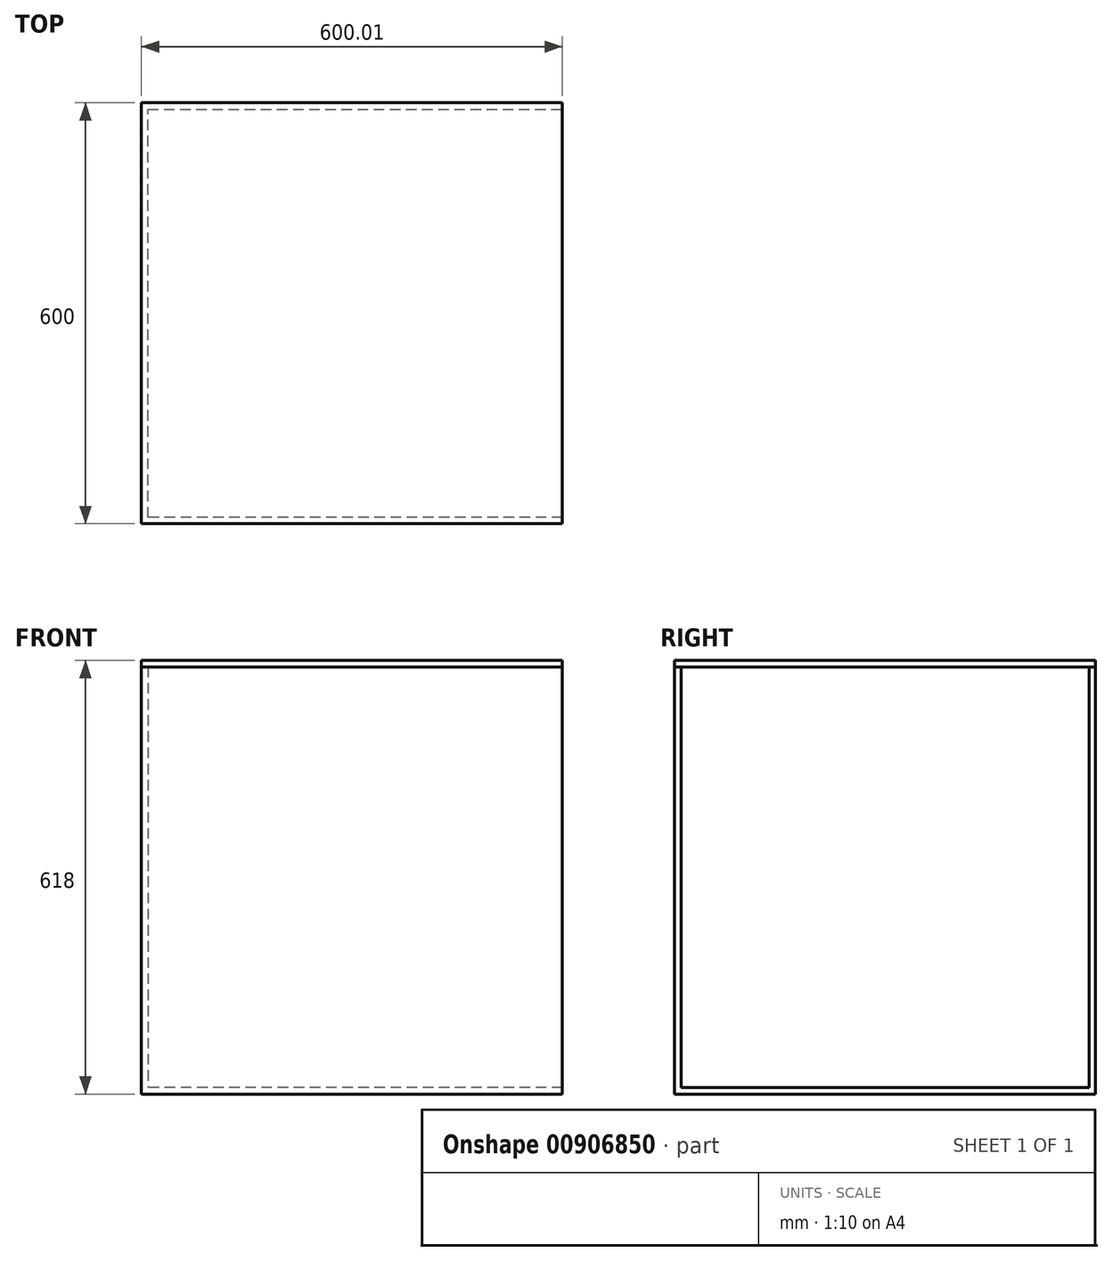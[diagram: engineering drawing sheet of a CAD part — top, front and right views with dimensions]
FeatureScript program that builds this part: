
annotation { "Feature Type Name" : "Feature", "Feature Type Description" : "" }
export const myFeature = defineFeature(function(context is Context, id is Id, definition is map)
    precondition{}
    {
        {
            var Q0;
            Q0=qCreatedBy(makeId("Top.planeOp"),FACE);
            var sketch = newSketch(context, id + "F0", { "sketchPlane" : qUnion([Q0])});
            skLineSegment(sketch, "E0.bottom", {"start": v(5.9, 0) * mm, "end": v(605.9, 0) * mm});
            skLineSegment(sketch, "E0.top", {"start": v(5.9, 600) * mm, "end": v(605.9, 600) * mm});
            skLineSegment(sketch, "E0.left", {"start": v(5.9, 0) * mm, "end": v(5.9, 600) * mm});
            skLineSegment(sketch, "E0.right", {"start": v(605.9, 0) * mm, "end": v(605.9, 600) * mm});
            skSolve(sketch);
        }
        {
            var Q0;
            Q0=makeQuery(id+"F0.imprint","IMPRINT",FACE,{"disambiguationData":[TD([[makeQuery(id+"F0.imprint","IMPRINT",EDGE,{"derivedFrom":sQuery(id+"F0.wireOp",EDGE,"E0.bottom")}),1.0]])]});
            extrude(context, id + "F1", {"entities" : qUnion([Q0]), "depth" : 9 * mm, "offsetDistance" : 25 * mm});
        }
        {
            var Q0;
            Q0=makeQuery(id+"F1.opExtrude","CAP_FACE",FACE,{"disambiguationData":[OSD([sQuery(id+"F0.wireOp",EDGE,"E0.bottom"),sQuery(id+"F0.wireOp",EDGE,"E0.top"),sQuery(id+"F0.wireOp",EDGE,"E0.left"),sQuery(id+"F0.wireOp",EDGE,"E0.right")])],"isStart":false});
            var sketch = newSketch(context, id + "F2", { "sketchPlane" : qUnion([Q0])});
            skLineSegment(sketch, "E1.bottom", {"start": v(5.9, 0) * mm, "end": v(14.9, 0) * mm});
            skLineSegment(sketch, "E1.top", {"start": v(5.9, 600) * mm, "end": v(14.9, 600) * mm});
            skLineSegment(sketch, "E1.left", {"start": v(5.9, 0) * mm, "end": v(5.9, 600) * mm});
            skLineSegment(sketch, "E1.right", {"start": v(14.9, 0) * mm, "end": v(14.9, 600) * mm});
            skSolve(sketch);
        }
        {
            var Q0;
            Q0 = qSketchRegion(id + "F2", true);
            extrude(context, id + "F3", {"entities" : qUnion([Q0]), "depth" : 600 * mm, "offsetDistance" : 25 * mm});
        }
        {
            var Q0;
            Q0=makeQuery(id+"F1.opExtrude","CAP_FACE",FACE,{"disambiguationData":[OSD([sQuery(id+"F0.wireOp",EDGE,"E0.bottom"),sQuery(id+"F0.wireOp",EDGE,"E0.top"),sQuery(id+"F0.wireOp",EDGE,"E0.left"),sQuery(id+"F0.wireOp",EDGE,"E0.right")])],"isStart":false});
            var sketch = newSketch(context, id + "F4", { "sketchPlane" : qUnion([Q0])});
            skLineSegment(sketch, "E2.bottom", {"start": v(14.9, 600) * mm, "end": v(605.9, 600) * mm});
            skLineSegment(sketch, "E2.top", {"start": v(14.9, 591) * mm, "end": v(605.9, 591) * mm});
            skLineSegment(sketch, "E2.left", {"start": v(14.9, 600) * mm, "end": v(14.9, 591) * mm});
            skLineSegment(sketch, "E2.right", {"start": v(605.9, 600) * mm, "end": v(605.9, 591) * mm});
            skSolve(sketch);
        }
        {
            var Q0;
            Q0 = qSketchRegion(id + "F4", true);
            extrude(context, id + "F5", {"entities" : qUnion([Q0]), "operationType" : NewBodyOperationType.ADD, "depth" : 600 * mm, "offsetDistance" : 25 * mm});
        }
        {
            var Q0;
            Q0=makeQuery(id+"F1.opExtrude","CAP_FACE",FACE,{"disambiguationData":[OSD([sQuery(id+"F0.wireOp",EDGE,"E0.bottom"),sQuery(id+"F0.wireOp",EDGE,"E0.top"),sQuery(id+"F0.wireOp",EDGE,"E0.left"),sQuery(id+"F0.wireOp",EDGE,"E0.right")])],"isStart":false});
            var sketch = newSketch(context, id + "F6", { "sketchPlane" : qUnion([Q0])});
            skLineSegment(sketch, "E3.bottom", {"start": v(605.9, 0) * mm, "end": v(14.9, 0) * mm});
            skLineSegment(sketch, "E3.left", {"start": v(605.9, 0) * mm, "end": v(605.9, 118.85) * mm});
            skLineSegment(sketch, "E3.right", {"start": v(14.9, 0) * mm, "end": v(14.9, 118.85) * mm});
            skLineSegment(sketch, "E4", {"start": v(605.9, 0) * mm, "end": v(605.9, 9) * mm});
            skLineSegment(sketch, "E5", {"start": v(605.9, 9) * mm, "end": v(0, 9) * mm});
            skSolve(sketch);
        }
        {
            var Q0;
            {var subQ0=sQuery(id+"F6.wireOp",EDGE,"E3.bottom");Q0=makeQuery(id+"F6.imprint","IMPRINT",FACE,{"disambiguationData":[TD([[makeQuery(id+"F6.imprint","IMPRINT",EDGE,{"derivedFrom":subQ0}),1.0]])]});}
            extrude(context, id + "F7", {"entities" : qUnion([Q0]), "operationType" : NewBodyOperationType.ADD, "depth" : 600 * mm, "offsetDistance" : 25 * mm});
        }
        {
            var Q0;
            Q0=makeQuery(id+"F7.opExtrude","CAP_FACE",FACE,{"disambiguationData":[OSD([sQuery(id+"F6.wireOp",EDGE,"E3.bottom"),sQuery(id+"F6.wireOp",EDGE,"E3.right"),sQuery(id+"F6.wireOp",EDGE,"E4"),sQuery(id+"F6.wireOp",EDGE,"E5")])],"isStart":false});
            var sketch = newSketch(context, id + "F8", { "sketchPlane" : qUnion([Q0])});
            skLineSegment(sketch, "E6.bottom", {"start": v(605.9, 0) * mm, "end": v(5.9, 0) * mm});
            skLineSegment(sketch, "E6.top", {"start": v(605.9, 600) * mm, "end": v(5.9, 600) * mm});
            skLineSegment(sketch, "E6.left", {"start": v(605.9, 0) * mm, "end": v(605.9, 600) * mm});
            skLineSegment(sketch, "E6.right", {"start": v(5.9, 0) * mm, "end": v(5.9, 600) * mm});
            skSolve(sketch);
        }
        {
            var Q0;
            Q0 = qSketchRegion(id + "F8", true);
            extrude(context, id + "F9", {"entities" : qUnion([Q0]), "depth" : 9 * mm, "offsetDistance" : 25 * mm});
        }
    });
